# Revit family: Zumtobel TECTON-V-MS
name_source: partatom
category: Lighting Fixtures
revit_build: Autodesk Revit 2016 (Build: 20150220_1215(x64)
units: mm (PartAtom-declared; Revit-internal decimal feet)

## family parameters
Always vertical = Yes
Cut with Voids When Loaded = No
Light Source = No
OmniClass Number = 23.80.70.11
OmniClass Title = Luminaries for Internal Lighting
Part Type = Normal
Room Calculation Point = No
Round Connector Dimension = Use Diameter
Shared = No
Work Plane-Based = No

## types (8) — shared parameters
Apparent Load = 0 VA
Assembly Code = D5020210
Body = ZG_Metal_White
Description = Tecton Connector
Height = 85 mm  [stored 0.278871 ft]
Length = 85 mm  [stored 0.278871 ft]
Manufacturer = Zumtobel Lighting
URL = http://www.zumtobel.com
Width = 85 mm  [stored 0.278871 ft]

## per-type parameters (varying)
| type | L1 | L2 | L3 320mm | L3 90mm | Model |
| TECTON T-VL1 WH | 90 mm | 90 mm | No | No | 22157273 |
| TECTON T-VT4 WH | 90 mm | 90 mm | Yes | No | 22157280 |
| TECTON T-VT3 WH | 90 mm | 320 mm  [stored 1.04987 ft] | Yes | No | 22157279 |
| TECTON T-VT2 WH | 320 mm  [stored 1.04987 ft] | 90 mm | No | Yes | 22157278 |
| TECTON T-VT1 WH | 320 mm  [stored 1.04987 ft] | 320 mm  [stored 1.04987 ft] | No | Yes | 22157277 |
| TECTON T-VL4 WH | 320 mm  [stored 1.04987 ft] | 320 mm  [stored 1.04987 ft] | No | No | 22157276 |
| TECTON T-VL3 WH | 320 mm  [stored 1.04987 ft] | 90 mm | No | No | 22157275 |
| TECTON T-VL2 WH | 90 mm | 320 mm  [stored 1.04987 ft] | No | No | 22157274 |

note: [stored X ft] marks values corroborated as IEEE doubles in the binary element streams (Revit-internal decimal feet)

## geometry (parser evidence)
native form markers: Sweep x3
no freeform markers — native parametric forms only
